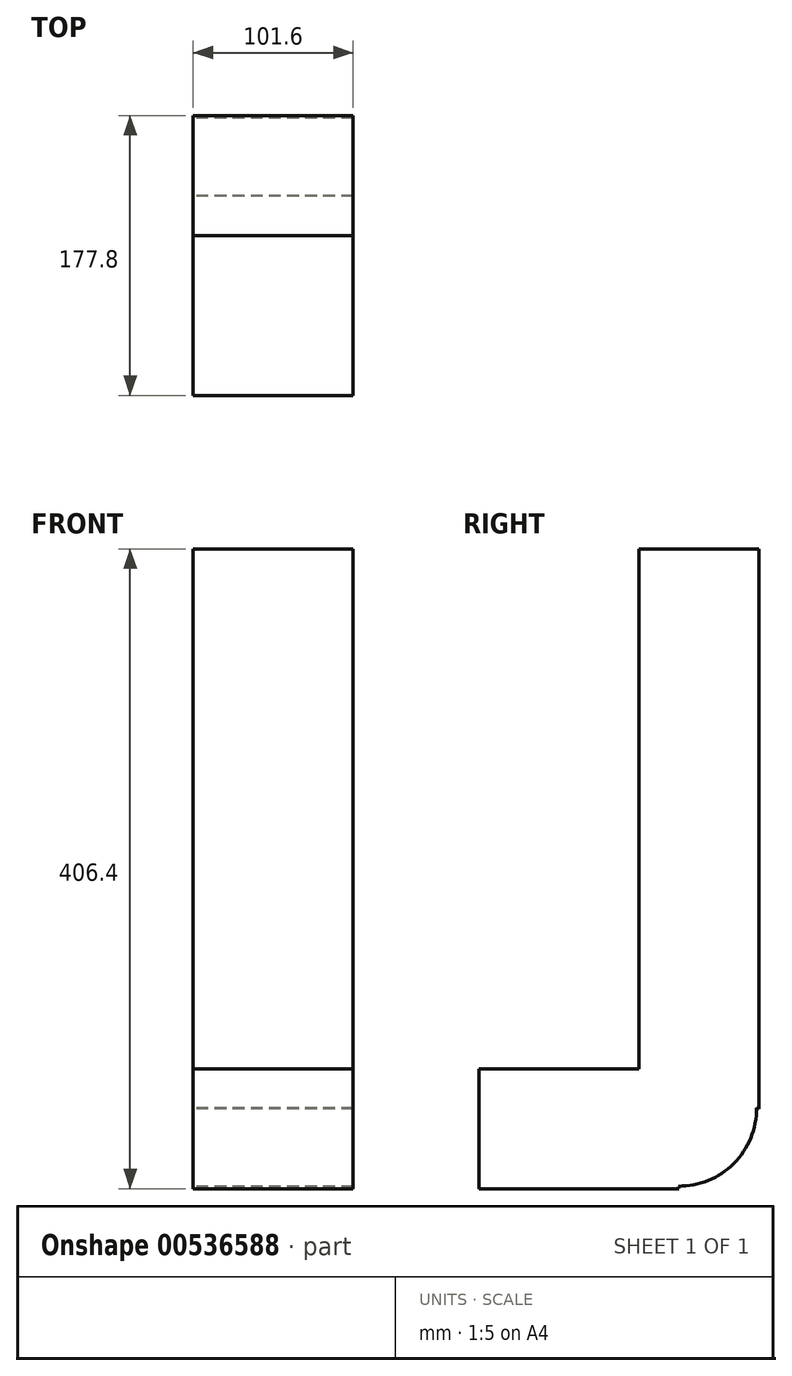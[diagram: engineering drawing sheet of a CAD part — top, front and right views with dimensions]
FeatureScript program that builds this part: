
annotation { "Feature Type Name" : "Feature", "Feature Type Description" : "" }
export const myFeature = defineFeature(function(context is Context, id is Id, definition is map)
    precondition{}
    {
        {
            var Q0;
            Q0=qCreatedBy(makeId("Right.planeOp"),FACE);
            var sketch = newSketch(context, id + "F0", { "sketchPlane" : qUnion([Q0])});
            skLineSegment(sketch, "E0.bottom", {"start": v(-141.48, 139.18) * mm, "end": v(-65.28, 139.18) * mm});
            skLineSegment(sketch, "E0.top", {"start": v(-141.48, -191.02) * mm, "end": v(-65.28, -191.02) * mm});
            skLineSegment(sketch, "E0.left", {"start": v(-141.48, 139.18) * mm, "end": v(-141.48, -191.02) * mm});
            skLineSegment(sketch, "E0.right", {"start": v(-65.28, 139.18) * mm, "end": v(-65.28, -191.02) * mm});
            skLineSegment(sketch, "E1.bottom", {"start": v(-65.28, -191.02) * mm, "end": v(-243.08, -191.02) * mm});
            skLineSegment(sketch, "E1.top", {"start": v(-116.08, -267.22) * mm, "end": v(-243.08, -267.22) * mm});
            skLineSegment(sketch, "E1.left", {"start": v(-65.28, -191.02) * mm, "end": v(-65.28, -216.42) * mm});
            skLineSegment(sketch, "E1.right", {"start": v(-243.08, -191.02) * mm, "end": v(-243.08, -267.22) * mm});
            skPoint(sketch, "E2.visualSharp", {"position": v(-65.28, -267.22) * mm});
            skArc(sketch, "E2.filletArc", {"start": v(-116.08, -267.22) * mm, "mid": v(-80.16, -252.34) * mm, "end": v(-65.28, -216.42) * mm});
            skSolve(sketch);
        }
        {
            var Q0;
            Q0 = qSketchRegion(id + "F0", true);
            extrude(context, id + "F1", {"entities" : qUnion([Q0]), "depth" : 101.6 * mm, "offsetDistance" : 25.4 * mm});
        }
        {
            var Q0;
            Q0=makeQuery(id+"F1.opExtrude","CAP_FACE",FACE,{"disambiguationData":[OSD([sQuery(id+"F0.wireOp",EDGE,"E0.bottom"),sQuery(id+"F0.wireOp",EDGE,"E0.left"),sQuery(id+"F0.wireOp",EDGE,"E0.right"),sQuery(id+"F0.wireOp",EDGE,"E1.bottom"),sQuery(id+"F0.wireOp",EDGE,"E1.top"),sQuery(id+"F0.wireOp",EDGE,"E1.left"),sQuery(id+"F0.wireOp",EDGE,"E1.right"),sQuery(id+"F0.wireOp",EDGE,"E2.filletArc")])],"isStart":true});
            var sketch = newSketch(context, id + "F2", { "sketchPlane" : qUnion([Q0])});
            skLineSegment(sketch, "E3", {"start": v(65.28, -216.42) * mm, "end": v(141.48, -191.02) * mm});
            skLineSegment(sketch, "E4", {"start": v(141.48, -191.02) * mm, "end": v(116.08, -267.22) * mm});
            skArc(sketch, "E5.0", {"start": v(116.08, -267.22) * mm, "mid": v(80.16, -252.34) * mm, "end": v(65.28, -216.42) * mm});
            skArc(sketch, "E6.0", {"start": v(116.61, -265.63) * mm, "mid": v(81.28, -251.22) * mm, "end": v(66.87, -215.9) * mm});
            skLineSegment(sketch, "E7.0", {"start": v(236.73, -197.37) * mm, "end": v(139.36, -197.37) * mm});
            skLineSegment(sketch, "E7.1", {"start": v(236.73, -260.87) * mm, "end": v(236.73, -197.37) * mm});
            skLineSegment(sketch, "E7.2", {"start": v(135.13, 132.83) * mm, "end": v(71.63, 132.83) * mm});
            skLineSegment(sketch, "E7.3", {"start": v(71.63, 132.83) * mm, "end": v(71.63, -216.42) * mm});
            skLineSegment(sketch, "E7.5", {"start": v(135.13, -193.14) * mm, "end": v(135.13, 132.83) * mm});
            skLineSegment(sketch, "E7.6", {"start": v(116.08, -260.87) * mm, "end": v(236.73, -260.87) * mm});
            skSolve(sketch);
        }
        {
            var Q0;
            {var subQ6=sQuery(id+"F2.wireOp",EDGE,"E6.0");Q0=makeQuery(id+"F2.imprint","IMPRINT",FACE,{"disambiguationData":[TD([[makeQuery(id+"F2.imprint","IMPRINT",EDGE,{"derivedFrom":subQ6}),-1.0]])]});}
            extrude(context, id + "F3", {"entities" : qUnion([Q0]), "operationType" : NewBodyOperationType.REMOVE, "endBound" : BoundingType.THROUGH_ALL, "oppositeDirection" : true, "depth" : 25.4 * mm, "offsetDistance" : 25.4 * mm});
        }
    });
